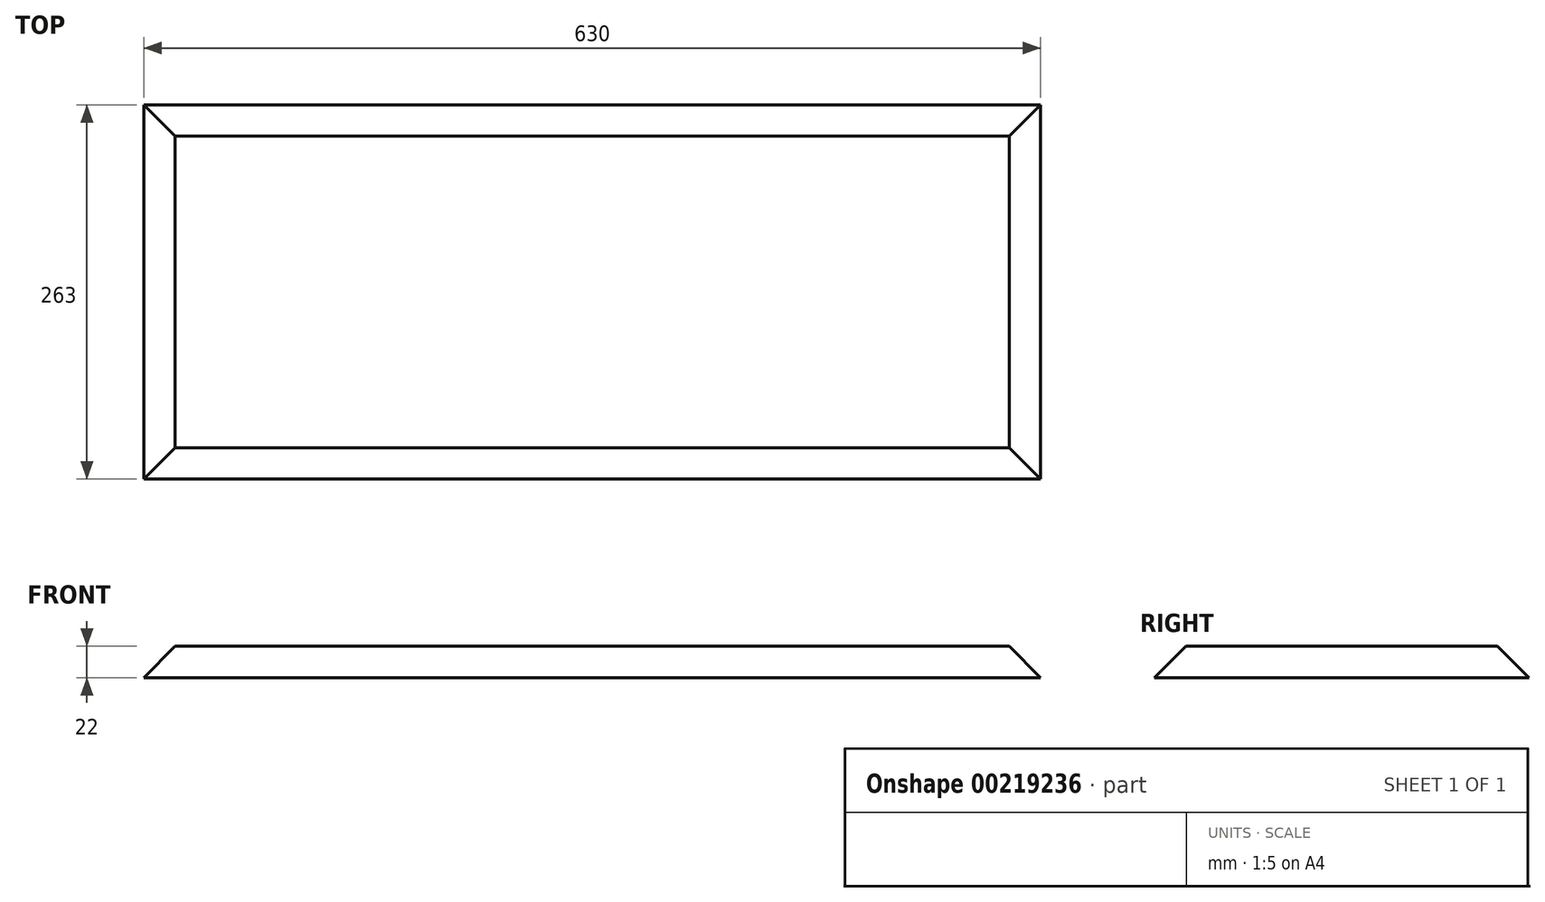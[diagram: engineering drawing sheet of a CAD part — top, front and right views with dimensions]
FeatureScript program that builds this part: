
annotation { "Feature Type Name" : "Feature", "Feature Type Description" : "" }
export const myFeature = defineFeature(function(context is Context, id is Id, definition is map)
    precondition{}
    {
        {
            var Q0;
            Q0=qCreatedBy(makeId("Top.planeOp"),FACE);
            var sketch = newSketch(context, id + "F0", { "sketchPlane" : qUnion([Q0])});
            skLineSegment(sketch, "E0.bottom", {"start": v(315, 131.5) * mm, "end": v(-315, 131.5) * mm});
            skLineSegment(sketch, "E0.top", {"start": v(315, -131.5) * mm, "end": v(-315, -131.5) * mm});
            skLineSegment(sketch, "E0.left", {"start": v(315, 131.5) * mm, "end": v(315, -131.5) * mm});
            skLineSegment(sketch, "E0.right", {"start": v(-315, 131.5) * mm, "end": v(-315, -131.5) * mm});
            skPoint(sketch, "E0.middle", {"position": v(0, 0) * mm});
            skSolve(sketch);
        }
        {
            var Q0;
            Q0=makeQuery(id+"F0.imprint","IMPRINT",FACE,{"disambiguationData":[TD([[makeQuery(id+"F0.imprint","IMPRINT",EDGE,{"derivedFrom":sQuery(id+"F0.wireOp",EDGE,"E0.bottom")}),1.0]])]});
            extrude(context, id + "F1", {"entities" : qUnion([Q0]), "depth" : 22 * mm});
        }
        {
            var Q0;
            Q0=makeQuery(id+"F1.opExtrude","CAP_EDGE",EDGE,{"disambiguationData":[OSD([sQuery(id+"F0.wireOp",EDGE,"E0.right")])],"isStart":false});
            var Q1;
            Q1=makeQuery(id+"F1.opExtrude","CAP_EDGE",EDGE,{"disambiguationData":[OSD([sQuery(id+"F0.wireOp",EDGE,"E0.bottom")])],"isStart":false});
            var Q2;
            Q2=makeQuery(id+"F1.opExtrude","CAP_EDGE",EDGE,{"disambiguationData":[OSD([sQuery(id+"F0.wireOp",EDGE,"E0.top")])],"isStart":false});
            var Q3;
            Q3=makeQuery(id+"F1.opExtrude","CAP_EDGE",EDGE,{"disambiguationData":[OSD([sQuery(id+"F0.wireOp",EDGE,"E0.left")])],"isStart":false});
            chamfer(context, id + "F2", {"entities" : qUnion([Q0, Q1, Q2, Q3]), "width" : 22 * mm, "tangentPropagation" : true});
        }
    });
